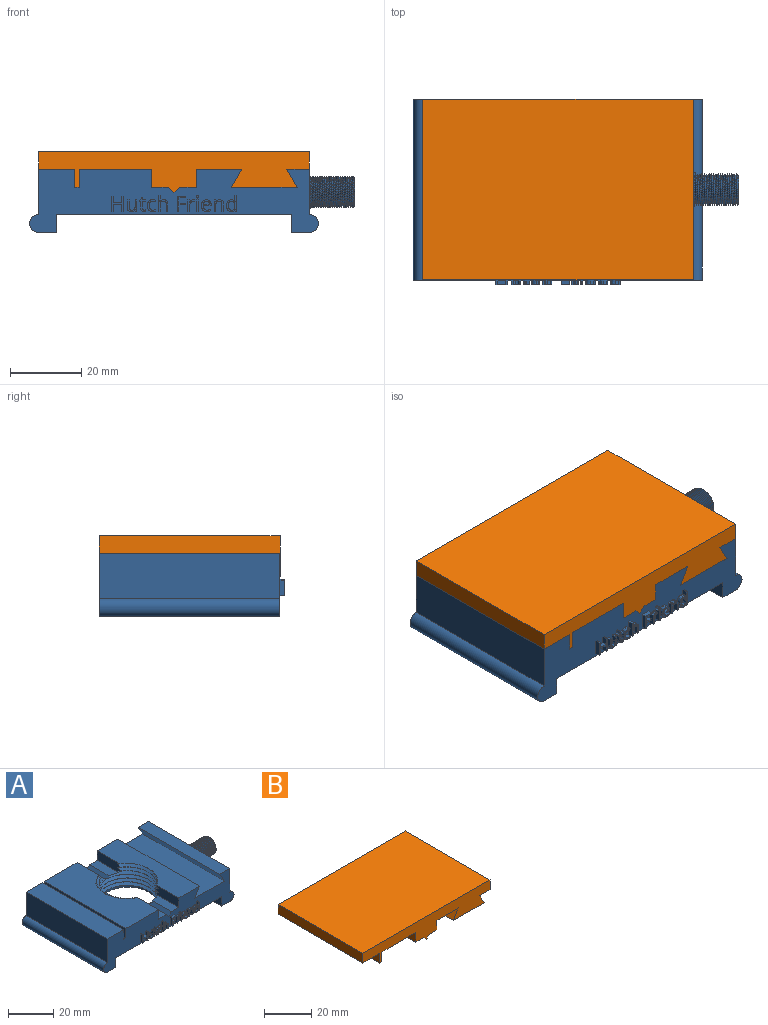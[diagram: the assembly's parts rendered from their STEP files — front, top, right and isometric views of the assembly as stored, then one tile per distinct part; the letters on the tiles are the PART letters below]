
ASSEMBLY  parts=2 mates=1
PART A: 264 faces, bbox 92x52.4x19.3 mm
  f0: cylinder r=12.7mm len=15.02mm, axis (0,0,-1), area 1.5mm2, adj f18,f23,f257,f259
  f1: cylinder r=12.7mm len=22mm, axis (0,0,-1), area 2.7mm2, adj f19,f22,f260,f262
  f2: cylinder r=12.7mm len=22mm, axis (0,0,-1), area 2.7mm2, adj f20,f23,f255,f258
  f3: cylinder r=12.7mm len=22mm, axis (0,0,-1), area 2.7mm2, adj f19,f22,f254,f261
  f4: cylinder r=12.7mm len=22mm, axis (0,0,-1), area 2.7mm2, adj f20,f23,f251,f256
  f5: cylinder r=12.7mm len=23.65mm, axis (0,0,-1), area 3.2mm2, adj f22,f43,f247,f253
  f6: cylinder r=12.7mm len=25.36mm, axis (0,0,-1), area 3.9mm2, adj f42,f45,f248,f252
  f7: plane 81.28x17.78mm, normal (0,-1,0), area 841.9mm2, adj f11,f12,f13,f14,f15,f16,f17,f18
  f8: cylinder r=12.7mm len=25.4mm, axis (0,0,-1), area 96.4mm2, adj f12,f44,f248,f249,f250
  f9: plane 81.28x17.78mm, normal (0,1,0), area 886.7mm2, adj f10,f12,f13,f14,f15,f16,f17,f18
  f10: plane 13.32x4.81mm, normal (0,0,1), area 59.4mm2, adj f9,f20,f42,f252
  f11: plane 13.21x4.83mm, normal (0,0,1), area 58.9mm2, adj f7,f23,f45,f251
  f12: plane 66.04x50.8mm, normal (0,0,-1), area 2848.1mm2, adj f7,f8,f9,f32,f34
  f13: plane 50.8x6.35mm, normal (0,0,1), area 322.6mm2, adj f7,f9,f16,f30
  f14: plane 51.12x20.64mm, normal (0,0,1), area 894.7mm2, adj f7,f9,f19,f22,f26,f262,f263
  f15: plane 50.8x10.16mm, normal (0,0,1), area 516.1mm2, adj f7,f9,f17,f25
  f16: plane 50.8x12.7mm, normal (1,0,0), area 510.6mm2, adj f7,f9,f13,f31,f36,f38,f40,f238
  f17: plane 50.8x12.7mm, normal (-1,0,0), area 645.2mm2, adj f7,f9,f15,f37
  f18: plane 51.04x12.94mm, normal (0,0,1), area 540.1mm2, adj f0,f7,f9,f20,f23,f28,f257,f259
  f19: plane 14.46x5.14mm, normal (1,0,0), area 68.2mm2, adj f1,f3,f9,f14,f21,f253,f254,f260
  f20: plane 14.46x5.14mm, normal (-1,0,0), area 68.2mm2, adj f2,f4,f9,f10,f18,f251,f252,f255
  f21: plane 14x4.87mm, normal (0,0,1), area 61.1mm2, adj f9,f19,f43,f253
  f22: plane 14.46x5.14mm, normal (1,0,0), area 69.1mm2, adj f1,f3,f5,f7,f14,f24,f247,f253
  f23: plane 14.46x5.14mm, normal (-1,0,0), area 69.1mm2, adj f0,f2,f4,f7,f11,f18,f251,f255
  f24: plane 13.86x4.85mm, normal (0,0,1), area 60.6mm2, adj f7,f22,f44,f247
  f25: plane 50.8x5.08mm, normal (1,0,0), area 258.1mm2, adj f7,f9,f15,f27
  f26: plane 50.8x5.08mm, normal (-1,0,0), area 258.1mm2, adj f7,f9,f14,f27
  f27: plane 50.8x1.27mm, normal (0,0,1), area 64.5mm2, adj f7,f9,f25,f26
  f28: plane 50.8x5.08mm, normal (0.87,0,-0.5), area 298mm2, adj f7,f9,f18,f29
  f29: plane 50.8x18.57mm, normal (0,0,1), area 943.1mm2, adj f7,f9,f28,f30
  f30: plane 50.8x5.08mm, normal (-0.87,0,-0.5), area 298mm2, adj f7,f9,f13,f29
  f31: cylinder r=4.76mm len=9.53mm, axis (-1,0,0), area 7.5mm2, adj f16,f236,f238
  f32: plane 50.8x5.08mm, normal (1,0,0), area 258.1mm2, adj f7,f9,f12,f33
  f33: plane 50.8x5.08mm, normal (0,0,-1), area 258.1mm2, adj f7,f9,f32,f37
  f34: plane 50.8x5.08mm, normal (-1,0,0), area 258.1mm2, adj f7,f9,f12,f35
  f35: plane 50.8x5.08mm, normal (0,0,-1), area 258.1mm2, adj f7,f9,f34,f36
  f36: cylinder r=2.54mm len=50.8mm, axis (0,-1,0), area 405.4mm2, adj f7,f9,f16,f35
  f37: cylinder r=2.54mm len=50.8mm, axis (0,-1,0), area 405.4mm2, adj f7,f9,f17,f33
  f38: cylinder r=3.17mm len=6.35mm, axis (1,0,0), area 50.7mm2, adj f16,f39
  f39: plane 6.35x6.35mm, normal (1,0,0), area 31.7mm2, adj f38
  f40: cylinder r=3.17mm len=6.35mm, axis (1,0,0), area 50.7mm2, adj f16,f41
  f41: plane 6.35x6.35mm, normal (1,0,0), area 31.7mm2, adj f40
  f42: plane 12.81x1.64mm, normal (-0.71,0,0.71), area 27mm2, adj f6,f9,f10,f43,f248,f249,f252
  f43: plane 12.82x1.65mm, normal (0.71,0,0.71), area 27mm2, adj f5,f9,f21,f42,f247,f249,f253
  f44: plane 12.75x1.63mm, normal (0.71,0,0.71), area 26.6mm2, adj f7,f8,f24,f45,f247,f248,f249
  f45: plane 12.75x1.64mm, normal (-0.71,0,0.71), area 26.6mm2, adj f6,f7,f11,f44,f248,f251,f252
  f46: plane 1.3x0.5mm, normal (0,0,-1), area 0.6mm2, adj f7,f47,f57,f58
  f47: plane 4.29x1.3mm, normal (1,0,0), area 5.6mm2, adj f7,f46,f48,f58
  f48: plane 1.3x0.5mm, normal (0,0,1), area 0.6mm2, adj f7,f47,f49,f58
  f49: plane 1.83x1.3mm, normal (-1,0,0), area 2.4mm2, adj f7,f48,f50,f58
  f50: plane 2.26x1.3mm, normal (0,0,1), area 2.9mm2, adj f7,f49,f51,f58
  f51: plane 1.83x1.3mm, normal (1,0,0), area 2.4mm2, adj f7,f50,f52,f58
  f52: plane 1.3x0.5mm, normal (0,0,1), area 0.6mm2, adj f7,f51,f53,f58
  f53: plane 4.29x1.3mm, normal (-1,0,0), area 5.6mm2, adj f7,f52,f54,f58
  f54: plane 1.3x0.5mm, normal (0,0,-1), area 0.6mm2, adj f7,f53,f55,f58
  f55: plane 2.02x1.3mm, normal (1,0,0), area 2.6mm2, adj f7,f54,f56,f58
  f56: plane 2.26x1.3mm, normal (0,0,-1), area 2.9mm2, adj f7,f55,f57,f58
  f57: plane 2.02x1.3mm, normal (-1,0,0), area 2.6mm2, adj f7,f46,f56,f58
  f58: plane 4.29x3.26mm, normal (0,-1,0), area 5.3mm2, adj f46,f47,f48,f49,f50,f51,f52,f53
  f59: plane 2.09x1.3mm, normal (1,0,0), area 2.7mm2, adj f7,f60,f75,f76
  f60: plane 1.3x0.49mm, normal (0,0,1), area 0.6mm2, adj f7,f59,f61,f76
  f61: plane 2.11x1.3mm, normal (-1,0,0), area 2.7mm2, adj f7,f60,f62,f76
  f62: extruded ~1.3x0.89mm, area 1.3mm2, adj f7,f61,f63,f76
  f63: extruded ~1.3x0.88mm, area 1.2mm2, adj f7,f62,f64,f76
  f64: extruded ~1.3x0.61mm, area 0.8mm2, adj f7,f63,f65,f76
  f65: extruded ~1.3x0.42mm, area 0.7mm2, adj f7,f64,f66,f76
  f66: plane 1.3x0.03mm, normal (0,0,-1), area 0mm2, adj f7,f65,f67,f76
  f67: plane 1.3x0.43mm, normal (-0.99,0,-0.16), area 0.6mm2, adj f7,f66,f68,f76
  f68: plane 1.3x0.4mm, normal (0,0,-1), area 0.5mm2, adj f7,f67,f69,f76
  f69: plane 3.22x1.3mm, normal (1,0,0), area 4.2mm2, adj f7,f68,f70,f76
  f70: plane 1.3x0.49mm, normal (0,0,1), area 0.6mm2, adj f7,f69,f71,f76
  f71: plane 1.69x1.3mm, normal (-1,0,0), area 2.2mm2, adj f7,f70,f72,f76
  f72: extruded ~1.3x0.9mm, area 1.2mm2, adj f7,f71,f73,f76
  f73: extruded ~1.3x0.74mm, area 1.1mm2, adj f7,f72,f74,f76
  f74: extruded ~1.3x0.56mm, area 0.8mm2, adj f7,f73,f75,f76
  f75: extruded ~1.3x0.59mm, area 0.8mm2, adj f7,f59,f74,f76
  f76: plane 3.28x2.69mm, normal (0,-1,0), area 3.8mm2, adj f59,f60,f61,f62,f63,f64,f65,f66
  f77: extruded ~1.3x0.25mm, area 0.3mm2, adj f7,f78,f95,f96
  f78: extruded ~1.3x0.38mm, area 0.5mm2, adj f7,f77,f79,f96
  f79: extruded ~1.3x0.45mm, area 0.6mm2, adj f7,f78,f80,f96
  f80: plane 1.89x1.3mm, normal (1,0,0), area 2.5mm2, adj f7,f79,f81,f96
  f81: plane 1.3x0.93mm, normal (0,0,-1), area 1.2mm2, adj f7,f80,f82,f96
  f82: plane 1.3x0.38mm, normal (1,0,0), area 0.5mm2, adj f7,f81,f83,f96
  f83: plane 1.3x0.93mm, normal (0,0,1), area 1.2mm2, adj f7,f82,f84,f96
  f84: plane 1.3x0.75mm, normal (1,0,0), area 1mm2, adj f7,f83,f85,f96
  f85: plane 1.3x0.28mm, normal (0,0,1), area 0.4mm2, adj f7,f84,f86,f96
  f86: plane 1.3x0.69mm, normal (-0.96,0,0.29), area 0.9mm2, adj f7,f85,f87,f96
  f87: plane 1.3x0.46mm, normal (-0.4,0,0.92), area 0.7mm2, adj f7,f86,f88,f96
  f88: plane 1.3x0.24mm, normal (-1,0,0), area 0.3mm2, adj f7,f87,f89,f96
  f89: plane 1.3x0.46mm, normal (0,0,-1), area 0.6mm2, adj f7,f88,f90,f96
  f90: plane 1.92x1.3mm, normal (-1,0,0), area 2.5mm2, adj f7,f89,f91,f96
  f91: extruded ~1.3x0.98mm, area 2mm2, adj f7,f90,f92,f96
  f92: extruded ~1.3x0.28mm, area 0.4mm2, adj f7,f91,f93,f96
  f93: extruded ~1.3x0.23mm, area 0.3mm2, adj f7,f92,f94,f96
  f94: plane 1.3x0.37mm, normal (1,0,0), area 0.5mm2, adj f7,f93,f95,f96
  f95: extruded ~1.3x0.19mm, area 0.3mm2, adj f7,f77,f94,f96
  f96: plane 4.02x1.91mm, normal (0,-1,0), area 2.7mm2, adj f77,f78,f79,f80,f81,f82,f83,f84
  f97: extruded ~1.3x1.08mm, area 1.6mm2, adj f7,f98,f111,f112
  f98: extruded ~1.3x0.81mm, area 1.1mm2, adj f7,f97,f99,f112
  f99: plane 1.3x0.43mm, normal (1,0,0), area 0.6mm2, adj f7,f98,f100,f112
  f100: extruded ~1.3x0.83mm, area 1.1mm2, adj f7,f99,f101,f112
  f101: extruded ~1.3x0.71mm, area 1mm2, adj f7,f100,f102,f112
  f102: extruded ~1.3x0.91mm, area 1.2mm2, adj f7,f101,f103,f112
  f103: extruded ~1.3x1.25mm, area 2.4mm2, adj f7,f102,f104,f112
  f104: extruded ~1.3x0.34mm, area 0.4mm2, adj f7,f103,f105,f112
  f105: extruded ~1.3x0.35mm, area 0.5mm2, adj f7,f104,f106,f112
  f106: plane 1.3x0.41mm, normal (0.94,0,-0.34), area 0.6mm2, adj f7,f105,f107,f112
  f107: extruded ~1.3x0.36mm, area 0.5mm2, adj f7,f106,f108,f112
  f108: extruded ~1.3x0.46mm, area 0.6mm2, adj f7,f107,f109,f112
  f109: extruded ~1.3x1.11mm, area 1.6mm2, adj f7,f108,f110,f112
  f110: extruded ~1.3x1.25mm, area 1.7mm2, adj f7,f109,f111,f112
  f111: extruded ~1.3x1.22mm, area 1.7mm2, adj f7,f97,f110,f112
  f112: plane 3.34x2.33mm, normal (0,-1,0), area 2.7mm2, adj f97,f98,f99,f100,f101,f102,f103,f104
  f113: plane 2.08x1.3mm, normal (-1,0,0), area 2.7mm2, adj f7,f114,f130,f131
  f114: plane 1.3x0.49mm, normal (0,0,-1), area 0.6mm2, adj f7,f113,f115,f131
  f115: plane 2.1x1.3mm, normal (1,0,0), area 2.7mm2, adj f7,f114,f116,f131
  f116: extruded ~1.3x0.89mm, area 1.3mm2, adj f7,f115,f117,f131
  f117: extruded ~1.3x0.89mm, area 1.2mm2, adj f7,f116,f118,f131
  f118: extruded ~1.3x0.61mm, area 0.8mm2, adj f7,f117,f119,f131
  f119: extruded ~1.3x0.41mm, area 0.7mm2, adj f7,f118,f120,f131
  f120: plane 1.3x0.03mm, normal (0,0,1), area 0mm2, adj f7,f119,f121,f131
  f121: extruded ~1.3x0.41mm, area 0.5mm2, adj f7,f120,f122,f131
  f122: plane 1.38x1.3mm, normal (1,0,0), area 1.8mm2, adj f7,f121,f123,f131
  f123: plane 1.3x0.49mm, normal (0,0,1), area 0.6mm2, adj f7,f122,f124,f131
  f124: plane 4.57x1.3mm, normal (-1,0,0), area 5.9mm2, adj f7,f123,f125,f131
  f125: plane 1.3x0.49mm, normal (0,0,-1), area 0.6mm2, adj f7,f124,f126,f131
  f126: plane 1.68x1.3mm, normal (1,0,0), area 2.2mm2, adj f7,f125,f127,f131
  f127: extruded ~1.3x0.9mm, area 1.2mm2, adj f7,f126,f128,f131
  f128: extruded ~1.3x0.74mm, area 1.1mm2, adj f7,f127,f129,f131
  f129: extruded ~1.3x0.56mm, area 0.8mm2, adj f7,f128,f130,f131
  f130: extruded ~1.3x0.59mm, area 0.8mm2, adj f7,f113,f129,f131
  f131: plane 4.57x2.69mm, normal (0,-1,0), area 4.4mm2, adj f113,f114,f115,f116,f117,f118,f119,f120
  f132: plane 1.3x0.5mm, normal (0,0,-1), area 0.6mm2, adj f7,f133,f141,f142
  f133: plane 1.84x1.3mm, normal (1,0,0), area 2.4mm2, adj f7,f132,f134,f142
  f134: plane 1.78x1.3mm, normal (0,0,-1), area 2.3mm2, adj f7,f133,f135,f142
  f135: plane 1.3x0.44mm, normal (1,0,0), area 0.6mm2, adj f7,f134,f136,f142
  f136: plane 1.78x1.3mm, normal (0,0,1), area 2.3mm2, adj f7,f135,f137,f142
  f137: plane 1.57x1.3mm, normal (1,0,0), area 2mm2, adj f7,f136,f138,f142
  f138: plane 1.89x1.3mm, normal (0,0,-1), area 2.5mm2, adj f7,f137,f139,f142
  f139: plane 1.3x0.44mm, normal (1,0,0), area 0.6mm2, adj f7,f138,f140,f142
  f140: plane 2.39x1.3mm, normal (0,0,1), area 3.1mm2, adj f7,f139,f141,f142
  f141: plane 4.29x1.3mm, normal (-1,0,0), area 5.6mm2, adj f7,f132,f140,f142
  f142: plane 4.29x2.39mm, normal (0,-1,0), area 3.8mm2, adj f132,f133,f134,f135,f136,f137,f138,f139
  f143: extruded ~1.3x0.38mm, area 0.5mm2, adj f7,f144,f155,f156
  f144: extruded ~1.3x0.56mm, area 0.8mm2, adj f7,f143,f145,f156
  f145: extruded ~1.3x0.48mm, area 0.9mm2, adj f7,f144,f146,f156
  f146: plane 1.3x0.02mm, normal (0,0,1), area 0mm2, adj f7,f145,f147,f156
  f147: plane 1.3x0.6mm, normal (1,0,0.09), area 0.8mm2, adj f7,f146,f148,f156
  f148: plane 1.3x0.4mm, normal (0,0,1), area 0.5mm2, adj f7,f147,f149,f156
  f149: plane 3.22x1.3mm, normal (-1,0,0), area 4.2mm2, adj f7,f148,f150,f156
  f150: plane 1.3x0.49mm, normal (0,0,-1), area 0.6mm2, adj f7,f149,f151,f156
  f151: plane 1.73x1.3mm, normal (1,0,0), area 2.2mm2, adj f7,f150,f152,f156
  f152: extruded ~1.3x0.79mm, area 1.1mm2, adj f7,f151,f153,f156
  f153: extruded ~1.3x0.67mm, area 1mm2, adj f7,f152,f154,f156
  f154: extruded ~1.3x0.35mm, area 0.5mm2, adj f7,f153,f155,f156
  f155: plane 1.3x0.45mm, normal (0.99,0,-0.15), area 0.6mm2, adj f7,f143,f154,f156
  f156: plane 3.28x1.85mm, normal (0,-1,0), area 2.2mm2, adj f143,f144,f145,f146,f147,f148,f149,f150
  f157: plane 1.3x0.49mm, normal (0,0,-1), area 0.6mm2, adj f7,f158,f160,f161
  f158: plane 3.22x1.3mm, normal (1,0,0), area 4.2mm2, adj f7,f157,f159,f161
  f159: plane 1.3x0.49mm, normal (0,0,1), area 0.6mm2, adj f7,f158,f160,f161
  f160: plane 3.22x1.3mm, normal (-1,0,0), area 4.2mm2, adj f7,f157,f159,f161
  f161: plane 3.22x0.49mm, normal (0,-1,0), area 1.6mm2, adj f157,f158,f159,f160
  f162: extruded ~1.3x0.25mm, area 0.3mm2, adj f7,f163,f169,f170
  f163: extruded ~1.3x0.25mm, area 0.3mm2, adj f7,f162,f164,f170
  f164: extruded ~1.3x0.21mm, area 0.3mm2, adj f7,f163,f165,f170
  f165: extruded ~1.3x0.2mm, area 0.3mm2, adj f7,f164,f166,f170
  f166: extruded ~1.3x0.25mm, area 0.3mm2, adj f7,f165,f167,f170
  f167: extruded ~1.3x0.24mm, area 0.3mm2, adj f7,f166,f168,f170
  f168: extruded ~1.3x0.2mm, area 0.3mm2, adj f7,f167,f169,f170
  f169: extruded ~1.3x0.21mm, area 0.3mm2, adj f7,f162,f168,f170
  f170: plane 0.65x0.58mm, normal (0,-1,0), area 0.3mm2, adj f162,f163,f164,f165,f166,f167,f168,f169
  f171: extruded ~1.3x0.62mm, area 0.9mm2, adj f172,f189,f190,f191
  f172: extruded ~1.3x0.59mm, area 0.9mm2, adj f171,f173,f190,f191
  f173: extruded ~1.3x0.71mm, area 1mm2, adj f172,f174,f190,f191
  f174: plane 1.68x1.3mm, normal (0,0,1), area 2.2mm2, adj f173,f189,f190,f191
  f175: extruded ~1.3x1.13mm, area 1.6mm2, adj f7,f176,f188,f190
  f176: extruded ~1.3x0.56mm, area 0.7mm2, adj f7,f175,f177,f190
  f177: extruded ~1.3x0.49mm, area 0.7mm2, adj f7,f176,f178,f190
  f178: plane 1.3x0.44mm, normal (1,0,0), area 0.6mm2, adj f7,f177,f179,f190
  f179: extruded ~1.3x1.03mm, area 1.4mm2, adj f7,f178,f180,f190
  f180: extruded ~1.3x0.77mm, area 1.1mm2, adj f7,f179,f181,f190
  f181: extruded ~1.3x0.86mm, area 1.2mm2, adj f7,f180,f182,f190
  f182: plane 2.22x1.3mm, normal (0,0,-1), area 2.9mm2, adj f7,f181,f183,f190
  f183: plane 1.3x0.31mm, normal (1,0,0), area 0.4mm2, adj f7,f182,f184,f190
  f184: extruded ~1.3x1.05mm, area 1.5mm2, adj f7,f183,f185,f190
  f185: extruded ~1.3x0.96mm, area 1.4mm2, adj f7,f184,f186,f190
  f186: extruded ~1.3x1.03mm, area 1.5mm2, adj f7,f185,f187,f190
  f187: extruded ~1.3x1.24mm, area 1.7mm2, adj f7,f186,f188,f190
  f188: extruded ~1.3x1.21mm, area 1.7mm2, adj f7,f175,f187,f190
  f189: extruded ~1.3x0.7mm, area 1mm2, adj f171,f174,f190,f191
  f190: plane 3.34x2.72mm, normal (0,-1,0), area 4.1mm2, adj f171,f172,f173,f174,f175,f176,f177,f178
  f191: plane 1.68x0.95mm, normal (0,-1,0), area 1.3mm2, adj f171,f172,f173,f174,f189
  f192: plane 2.08x1.3mm, normal (-1,0,0), area 2.7mm2, adj f7,f193,f208,f209
  f193: plane 1.3x0.49mm, normal (0,0,-1), area 0.6mm2, adj f7,f192,f194,f209
  f194: plane 2.1x1.3mm, normal (1,0,0), area 2.7mm2, adj f7,f193,f195,f209
  f195: extruded ~1.3x0.9mm, area 1.3mm2, adj f7,f194,f196,f209
  f196: extruded ~1.3x0.88mm, area 1.2mm2, adj f7,f195,f197,f209
  f197: extruded ~1.3x0.6mm, area 0.8mm2, adj f7,f196,f198,f209
  f198: extruded ~1.3x0.42mm, area 0.7mm2, adj f7,f197,f199,f209
  f199: plane 1.3x0.02mm, normal (0,0,1), area 0mm2, adj f7,f198,f200,f209
  f200: plane 1.3x0.44mm, normal (0.98,0,0.18), area 0.6mm2, adj f7,f199,f201,f209
  f201: plane 1.3x0.4mm, normal (0,0,1), area 0.5mm2, adj f7,f200,f202,f209
  f202: plane 3.22x1.3mm, normal (-1,0,0), area 4.2mm2, adj f7,f201,f203,f209
  f203: plane 1.3x0.49mm, normal (0,0,-1), area 0.6mm2, adj f7,f202,f204,f209
  f204: plane 1.69x1.3mm, normal (1,0,0), area 2.2mm2, adj f7,f203,f205,f209
  f205: extruded ~1.3x0.9mm, area 1.2mm2, adj f7,f204,f206,f209
  f206: extruded ~1.3x0.74mm, area 1.1mm2, adj f7,f205,f207,f209
  f207: extruded ~1.3x0.56mm, area 0.8mm2, adj f7,f206,f208,f209
  f208: extruded ~1.3x0.59mm, area 0.8mm2, adj f7,f192,f207,f209
  f209: plane 3.28x2.69mm, normal (0,-1,0), area 3.8mm2, adj f192,f193,f194,f195,f196,f197,f198,f199
  f210: extruded ~1.3x0.72mm, area 1mm2, adj f211,f233,f234,f235
  f211: extruded ~1.3x0.66mm, area 1mm2, adj f210,f212,f234,f235
  f212: extruded ~1.3x0.93mm, area 1.3mm2, adj f211,f213,f234,f235
  f213: extruded ~1.3x0.94mm, area 1.3mm2, adj f212,f214,f234,f235
  f214: extruded ~1.3x0.66mm, area 1mm2, adj f213,f215,f234,f235
  f215: extruded ~1.3x0.73mm, area 1.1mm2, adj f214,f216,f234,f235
  f216: extruded ~1.3x0.98mm, area 1.3mm2, adj f215,f217,f234,f235
  f217: plane 1.3x0.1mm, normal (-1,0,0), area 0.1mm2, adj f216,f233,f234,f235
  f218: plane 1.3x0.03mm, normal (0,0,-1), area 0mm2, adj f7,f219,f232,f234
  f219: plane 1.3x0.43mm, normal (-0.99,0,-0.15), area 0.6mm2, adj f7,f218,f220,f234
  f220: plane 1.3x0.4mm, normal (0,0,-1), area 0.5mm2, adj f7,f219,f221,f234
  f221: plane 4.57x1.3mm, normal (1,0,0), area 5.9mm2, adj f7,f220,f222,f234
  f222: plane 1.3x0.49mm, normal (0,0,1), area 0.6mm2, adj f7,f221,f223,f234
  f223: plane 1.31x1.3mm, normal (-1,0,0), area 1.7mm2, adj f7,f222,f224,f234
  f224: plane 1.3x0.23mm, normal (-1,0,-0.05), area 0.3mm2, adj f7,f223,f225,f234
  f225: plane 1.3x0.23mm, normal (-1,0,-0.09), area 0.3mm2, adj f7,f224,f226,f234
  f226: plane 1.3x0.04mm, normal (0,0,1), area 0.1mm2, adj f7,f225,f227,f234
  f227: extruded ~1.3x1mm, area 1.5mm2, adj f7,f226,f228,f234
  f228: extruded ~1.3x0.98mm, area 1.4mm2, adj f7,f227,f229,f234
  f229: extruded ~1.3x1.24mm, area 1.7mm2, adj f7,f228,f230,f234
  f230: extruded ~1.3x1.23mm, area 1.7mm2, adj f7,f229,f231,f234
  f231: extruded ~1.3x0.98mm, area 1.4mm2, adj f7,f230,f232,f234
  f232: extruded ~1.3x1.01mm, area 1.5mm2, adj f7,f218,f231,f234
  f233: extruded ~1.3x0.88mm, area 1.2mm2, adj f210,f217,f234,f235
  f234: plane 4.63x2.83mm, normal (0,-1,0), area 5mm2, adj f210,f211,f212,f213,f214,f215,f216,f217
  f235: plane 2.52x1.84mm, normal (0,-1,0), area 3.9mm2, adj f210,f211,f212,f213,f214,f215,f216,f217
  f236: plane 0.7x0.63mm, normal (0,-0.59,0.81), area 0.3mm2, adj f31,f237,f238,f239
  f237: bspline ~12.55x8.26mm, area 323.1mm2, adj f236,f238,f239,f245,f246
  f238: bspline ~9.52x9.51mm, area 11.5mm2, adj f16,f31,f236,f237
  f239: bspline ~12.58x10.2mm, area 316.2mm2, adj f236,f237,f245,f246
  f240: plane 5.08x5.08mm, normal (1,0,0), area 25.8mm2, adj f241,f242,f243,f244
  f241: plane 12.7x5.08mm, normal (0,1,0), area 64.5mm2, adj f240,f242,f244,f246
  f242: plane 12.7x5.08mm, normal (0,0,1), area 64.5mm2, adj f240,f241,f243,f246
  f243: plane 12.7x5.08mm, normal (0,-1,0), area 64.5mm2, adj f240,f242,f244,f246
  f244: plane 12.7x5.08mm, normal (0,0,-1), area 64.5mm2, adj f240,f241,f243,f246
  f245: cone r=4.06mm half-angle=45deg, axis (-1,0,0), area 5.4mm2, adj f237,f239,f246
  f246: plane 8.16x8.16mm, normal (1,0,0), area 25.9mm2, adj f237,f239,f241,f242,f243,f244,f245
  f247: bspline ~33.13x21.52mm, area 72.9mm2, adj f5,f22,f24,f43,f44,f249
  f248: bspline ~33.13x28.69mm, area 418.7mm2, adj f6,f8,f42,f44,f45,f249,f250
  f249: bspline ~33.13x28.69mm, area 499.6mm2, adj f8,f42,f43,f44,f247,f248,f250
  f250: plane 1.9x1.34mm, normal (0.81,-0.59,0), area 1.6mm2, adj f8,f248,f249
  f251: bspline ~33.13x21.52mm, area 59.5mm2, adj f4,f11,f20,f23,f45,f252
  f252: bspline ~33.13x21.52mm, area 72.4mm2, adj f6,f10,f20,f42,f45,f251
  f253: bspline ~33.13x21.52mm, area 58.9mm2, adj f5,f19,f21,f22,f43,f254
  f254: bspline ~33.13x21.52mm, area 55.5mm2, adj f3,f19,f22,f253
  f255: bspline ~33.13x21.52mm, area 55.5mm2, adj f2,f20,f23,f256
  f256: bspline ~33.13x21.52mm, area 55.5mm2, adj f4,f20,f23,f255
  f257: bspline ~33.13x21.52mm, area 53.4mm2, adj f0,f18,f20,f23,f258
  f258: bspline ~33.13x21.52mm, area 55.5mm2, adj f2,f20,f23,f257
  f259: bspline ~21.52x16.56mm, area 4.6mm2, adj f0,f18,f23
  f260: bspline ~33.13x21.52mm, area 55.5mm2, adj f1,f19,f22,f261
  f261: bspline ~33.13x21.52mm, area 55.5mm2, adj f3,f19,f22,f260
  f262: bspline ~33.13x21.52mm, area 51.6mm2, adj f1,f14,f19,f22,f263
  f263: bspline ~28.99x21.52mm, area 7.1mm2, adj f14,f19,f262
PART B: 46 faces, bbox 76.3x50.9x12.4 mm
  f0: cylinder r=12.7mm len=12.7mm, axis (0,0,-1), area 1.3mm2, adj f10,f12,f38,f41
  f1: cylinder r=12.7mm len=1.2mm, axis (0,0,-1), area 0.1mm2, adj f6,f27,f34,f36
  f2: cylinder r=12.7mm len=7.91mm, axis (0,0,-1), area 0.8mm2, adj f7,f8,f10,f26,f37,f40,f45
  f3: cylinder r=12.7mm len=12.7mm, axis (0,0,-1), area 1.3mm2, adj f9,f11,f33,f43
  f4: cylinder r=12.7mm len=25.4mm, axis (0,0,-1), area 310.3mm2, adj f9,f10,f11,f12,f13,f14,f32,f42
  f5: plane 14.1x4.76mm, normal (0,0,-1), area 63.1mm2, adj f12,f21,f26,f37
  f6: plane 12.76x1.64mm, normal (-0.71,0,-0.71), area 27.1mm2, adj f1,f20,f25,f27,f33,f34,f36
  f7: plane 12.86x1.65mm, normal (0.71,0,-0.71), area 26.5mm2, adj f2,f8,f21,f26,f39,f40
  f8: plane 14.28x4.8mm, normal (0,0,-1), area 63.7mm2, adj f2,f7,f10,f21,f45
  f9: plane 14.46x5.14mm, normal (1,0,0), area 70.8mm2, adj f3,f4,f13,f20,f28,f33,f43,f44
  f10: plane 14.46x5.14mm, normal (1,0,0), area 69.6mm2, adj f0,f2,f4,f8,f13,f21,f37,f38
  f11: plane 14.46x5.14mm, normal (-1,0,0), area 70.3mm2, adj f3,f4,f14,f20,f25,f33,f35,f43
  f12: plane 14.46x5.14mm, normal (-1,0,0), area 69.6mm2, adj f0,f4,f5,f14,f21,f37,f38,f41
  f13: plane 50.8x12.7mm, normal (0,0,-1), area 546.1mm2, adj f4,f9,f10,f20,f21,f29
  f14: plane 50.8x20.32mm, normal (0,0,-1), area 933.2mm2, adj f4,f11,f12,f20,f21,f24
  f15: plane 50.8x10.16mm, normal (0,0,-1), area 516.1mm2, adj f17,f20,f21,f22
  f16: plane 76.2x50.8mm, normal (0,0,1), area 3871mm2, adj f17,f19,f20,f21
  f17: plane 50.8x5mm, normal (-1,0,0), area 254mm2, adj f15,f16,f20,f21
  f18: plane 50.8x6.35mm, normal (0,0,-1), area 322.6mm2, adj f19,f20,f21,f31
  f19: plane 50.8x5mm, normal (1,0,0), area 254mm2, adj f16,f18,f20,f21
  f20: plane 76.2x11.67mm, normal (0,1,0), area 533.9mm2, adj f6,f9,f11,f13,f14,f15,f16,f17
  f21: plane 76.2x11.67mm, normal (0,-1,0), area 533.9mm2, adj f5,f7,f8,f10,f12,f13,f14,f15
  f22: plane 50.8x5.08mm, normal (-1,0,0), area 258.1mm2, adj f15,f20,f21,f23
  f23: plane 50.8x1.27mm, normal (0,0,-1), area 64.5mm2, adj f20,f21,f22,f24
  f24: plane 50.8x5.08mm, normal (1,0,0), area 258.1mm2, adj f14,f20,f21,f23
  f25: plane 12.83x4.84mm, normal (0,0,-1), area 56.2mm2, adj f6,f11,f20,f33,f35
  f26: plane 12.86x1.65mm, normal (-0.71,0,-0.71), area 26.6mm2, adj f2,f5,f7,f21,f37,f39,f40
  f27: plane 12.76x1.63mm, normal (0.71,0,-0.71), area 27mm2, adj f1,f6,f20,f28,f33,f34,f36
  f28: plane 12.9x4.76mm, normal (0,0,-1), area 56.8mm2, adj f9,f20,f27,f33
  f29: plane 50.8x5.08mm, normal (-0.87,0,0.5), area 298mm2, adj f13,f20,f21,f30
  f30: plane 50.8x18.57mm, normal (0,0,-1), area 943.1mm2, adj f20,f21,f29,f31
  f31: plane 50.8x5.08mm, normal (0.87,0,0.5), area 298mm2, adj f18,f20,f21,f30
  f32: plane 25.4x25.4mm, normal (0,0,-1), area 506.7mm2, adj f4
  f33: bspline ~21.52x16.56mm, area 23.8mm2, adj f3,f6,f9,f11,f25,f27,f28,f34
  f34: bspline ~14.35x5.57mm, area 4mm2, adj f1,f6,f27,f33
  f35: bspline ~14.35x5.57mm, area 0.5mm2, adj f11,f25,f33
  f36: bspline ~14.35x5.57mm, area 0.5mm2, adj f1,f6,f27
  f37: bspline ~21.52x16.56mm, area 24.3mm2, adj f2,f5,f10,f12,f26,f38
  f38: bspline ~28.69x16.56mm, area 25.2mm2, adj f0,f10,f12,f37
  f39: bspline ~14.35x5.57mm, area 0.6mm2, adj f7,f26,f40
  f40: bspline ~14.35x5.57mm, area 4mm2, adj f2,f7,f26,f39
  f41: bspline ~14.35x3.35mm, area 25.2mm2, adj f0,f10,f12,f42
  f42: bspline ~21.52x16.56mm, area 25.2mm2, adj f4,f10,f12,f41
  f43: bspline ~21.52x16.56mm, area 25.2mm2, adj f3,f9,f11,f44
  f44: bspline ~21.52x16.56mm, area 25.2mm2, adj f4,f9,f11,f43
  f45: bspline ~14.35x5.57mm, area 0.3mm2, adj f2,f8,f10
PLACE A t=(17.79,23.33,-20.57)mm
PLACE B t=(17.79,-2.09,-2.87)mm
MATE slider B.f21 <-> A.f7  axis (0,-1,0) through (-20.31,-2.09,-7.87)mm
